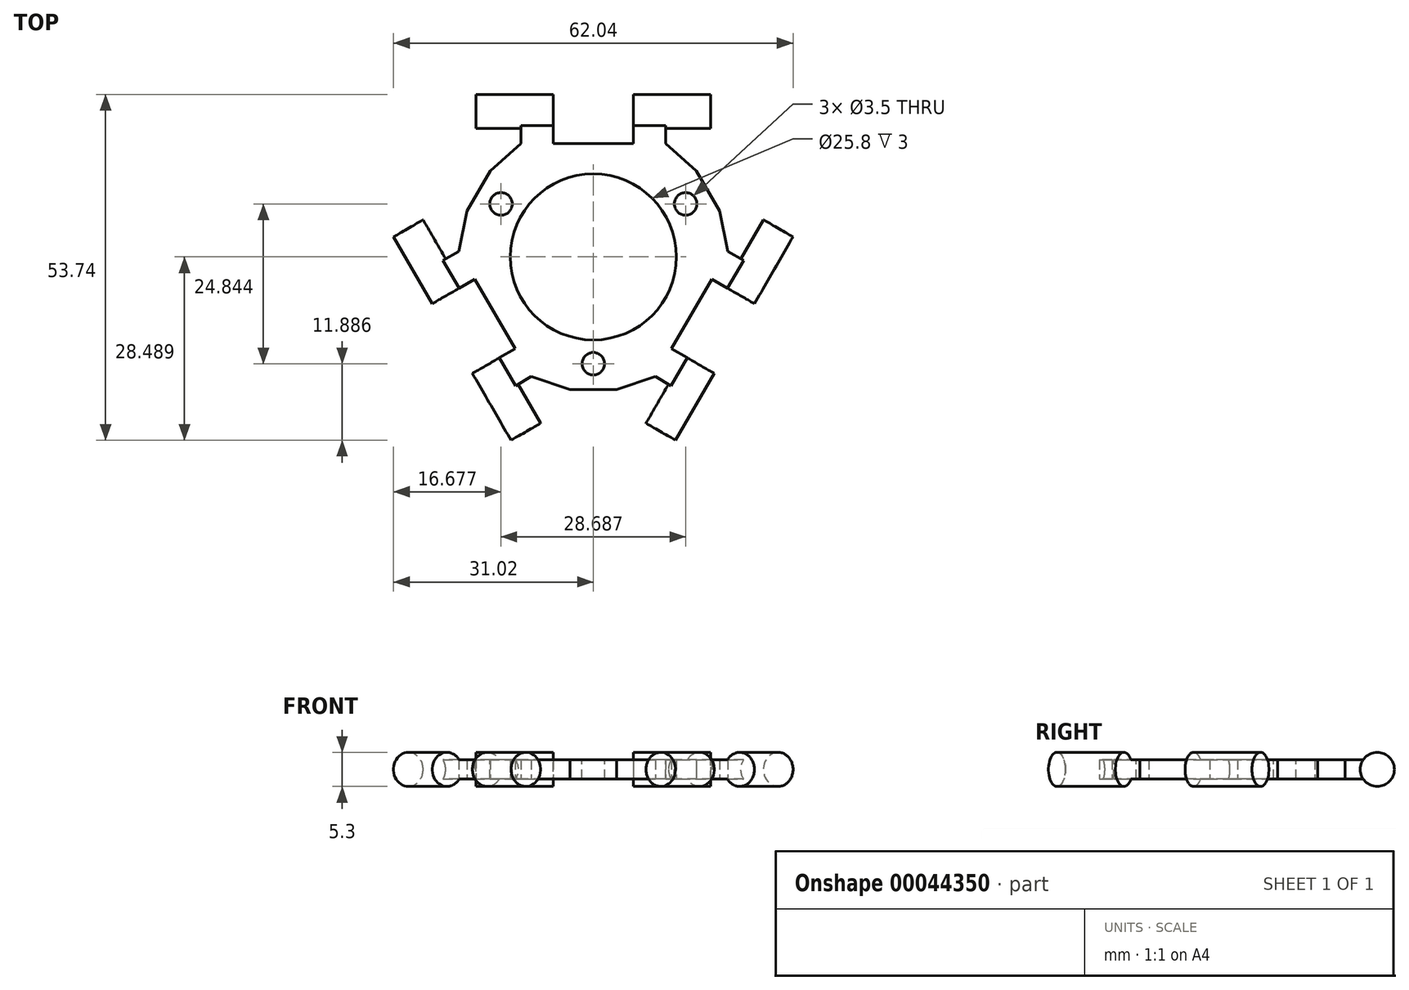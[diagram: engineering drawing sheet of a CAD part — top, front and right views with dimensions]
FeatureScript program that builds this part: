
annotation { "Feature Type Name" : "Feature", "Feature Type Description" : "" }
export const myFeature = defineFeature(function(context is Context, id is Id, definition is map)
    precondition{}
    {
        {
            var Q0;
            Q0=qCreatedBy(makeId("Top.planeOp"),FACE);
            var sketch = newSketch(context, id + "F0", { "sketchPlane" : qUnion([Q0])});
            skLineSegment(sketch, "E0", {"start": v(11.25, 26.96) * mm, "end": v(11.25, 31.96) * mm});
            skLineSegment(sketch, "E1", {"start": v(11.25, 31.96) * mm, "end": v(6.25, 31.96) * mm});
            skLineSegment(sketch, "E2", {"start": v(6.25, 31.96) * mm, "end": v(6.25, 26.96) * mm});
            skLineSegment(sketch, "E3", {"start": v(6.25, 26.96) * mm, "end": v(-6.25, 26.96) * mm});
            skLineSegment(sketch, "E4", {"start": v(-6.25, 26.96) * mm, "end": v(-6.25, 31.96) * mm});
            skLineSegment(sketch, "E5", {"start": v(-6.25, 31.96) * mm, "end": v(-11.25, 31.96) * mm});
            skLineSegment(sketch, "E6", {"start": v(-11.25, 31.96) * mm, "end": v(-11.25, 26.96) * mm});
            skLineSegment(sketch, "E7", {"start": v(11.25, 26.96) * mm, "end": v(16, 22.72) * mm});
            skLineSegment(sketch, "E8", {"start": v(-11.25, 26.96) * mm, "end": v(-16, 22.72) * mm});
            skLineSegment(sketch, "E9", {"start": v(16, 22.72) * mm, "end": v(19.6, 16.48) * mm});
            skLineSegment(sketch, "E10", {"start": v(-16, 22.72) * mm, "end": v(-19.6, 16.48) * mm});
            skLineSegment(sketch, "E11", {"start": v(-19.6, 16.48) * mm, "end": v(-20.9, 10.24) * mm});
            skLineSegment(sketch, "E12", {"start": v(19.6, 16.48) * mm, "end": v(20.9, 10.24) * mm});
            skLineSegment(sketch, "E13", {"start": v(-20.9, 10.24) * mm, "end": v(-25.23, 7.74) * mm});
            skLineSegment(sketch, "E14", {"start": v(-25.23, 7.74) * mm, "end": v(-22.73, 3.41) * mm});
            skLineSegment(sketch, "E15", {"start": v(-22.73, 3.41) * mm, "end": v(-18.4, 5.91) * mm});
            skLineSegment(sketch, "E16", {"start": v(-18.4, 5.91) * mm, "end": v(-12.15, -4.91) * mm});
            skLineSegment(sketch, "E17", {"start": v(-12.15, -4.91) * mm, "end": v(-16.48, -7.41) * mm});
            skLineSegment(sketch, "E18", {"start": v(-16.48, -7.41) * mm, "end": v(-13.98, -11.74) * mm});
            skLineSegment(sketch, "E19", {"start": v(-13.98, -11.74) * mm, "end": v(-9.65, -9.24) * mm});
            skLineSegment(sketch, "E20", {"start": v(20.9, 10.24) * mm, "end": v(25.23, 7.74) * mm});
            skLineSegment(sketch, "E21", {"start": v(25.23, 7.74) * mm, "end": v(22.73, 3.41) * mm});
            skLineSegment(sketch, "E22", {"start": v(22.73, 3.41) * mm, "end": v(18.4, 5.91) * mm});
            skLineSegment(sketch, "E23", {"start": v(18.4, 5.91) * mm, "end": v(12.15, -4.91) * mm});
            skLineSegment(sketch, "E24", {"start": v(12.15, -4.91) * mm, "end": v(16.48, -7.41) * mm});
            skLineSegment(sketch, "E25", {"start": v(16.48, -7.41) * mm, "end": v(13.98, -11.74) * mm});
            skLineSegment(sketch, "E26", {"start": v(13.98, -11.74) * mm, "end": v(9.65, -9.24) * mm});
            skLineSegment(sketch, "E27", {"start": v(-9.65, -9.24) * mm, "end": v(-3.6, -11.24) * mm});
            skLineSegment(sketch, "E28", {"start": v(-3.6, -11.24) * mm, "end": v(3.6, -11.24) * mm});
            skLineSegment(sketch, "E29", {"start": v(3.6, -11.24) * mm, "end": v(9.65, -9.24) * mm});
            skPoint(sketch, "E30.first.point", {"position": v(0, 26.96) * mm});
            skPoint(sketch, "E30.second.point", {"position": v(15.27, 0.5) * mm});
            skPoint(sketch, "E30.third.point", {"position": v(-15.27, 0.5) * mm});
            skCircle(sketch, "E31", {"center": v(0, 9.36) * mm, "radius": 12.9 * mm});
            skLineSegment(sketch, "E32", {"start": v(-17.8, 19.6) * mm, "end": v(15.27, 0.5) * mm, "construction": true});
            skLineSegment(sketch, "E33", {"start": v(17.8, 19.6) * mm, "end": v(-15.27, 0.5) * mm, "construction": true});
            skLineSegment(sketch, "E34", {"start": v(0, -11.24) * mm, "end": v(0, 26.96) * mm, "construction": true});
            skSolve(sketch);
        }
        {
            var Q0;
            Q0=qSketchRegion(id+"F0",true);
            extrude(context, id + "F1", {"entities" : qUnion([Q0]), "depth" : 3 * mm});
        }
        {
            var Q0;
            Q0=makeQuery(id+"F1.opExtrude","CAP_FACE",FACE,{"disambiguationData":[OSD([sQuery(id+"F0.wireOp",EDGE,"E0"),sQuery(id+"F0.wireOp",EDGE,"E1"),sQuery(id+"F0.wireOp",EDGE,"E2"),sQuery(id+"F0.wireOp",EDGE,"E3"),sQuery(id+"F0.wireOp",EDGE,"E4"),sQuery(id+"F0.wireOp",EDGE,"E5"),sQuery(id+"F0.wireOp",EDGE,"E6"),sQuery(id+"F0.wireOp",EDGE,"E7"),sQuery(id+"F0.wireOp",EDGE,"E8"),sQuery(id+"F0.wireOp",EDGE,"E9"),sQuery(id+"F0.wireOp",EDGE,"E10"),sQuery(id+"F0.wireOp",EDGE,"E11"),sQuery(id+"F0.wireOp",EDGE,"E12"),sQuery(id+"F0.wireOp",EDGE,"E13"),sQuery(id+"F0.wireOp",EDGE,"E14"),sQuery(id+"F0.wireOp",EDGE,"E15"),sQuery(id+"F0.wireOp",EDGE,"E16"),sQuery(id+"F0.wireOp",EDGE,"E17"),sQuery(id+"F0.wireOp",EDGE,"E18"),sQuery(id+"F0.wireOp",EDGE,"E19"),sQuery(id+"F0.wireOp",EDGE,"E20"),sQuery(id+"F0.wireOp",EDGE,"E21"),sQuery(id+"F0.wireOp",EDGE,"E22"),sQuery(id+"F0.wireOp",EDGE,"E23"),sQuery(id+"F0.wireOp",EDGE,"E24"),sQuery(id+"F0.wireOp",EDGE,"E25"),sQuery(id+"F0.wireOp",EDGE,"E26"),sQuery(id+"F0.wireOp",EDGE,"E27"),sQuery(id+"F0.wireOp",EDGE,"E28"),sQuery(id+"F0.wireOp",EDGE,"E29"),sQuery(id+"F0.wireOp",EDGE,"E31")])],"isStart":false});
            var sketch = newSketch(context, id + "F2", { "sketchPlane" : qUnion([Q0])});
            skCircle(sketch, "E35", {"center": v(-14.34, 17.6) * mm, "radius": 1.75 * mm});
            skCircle(sketch, "E36", {"center": v(14.34, 17.6) * mm, "radius": 1.75 * mm});
            skCircle(sketch, "E37", {"center": v(0, -7.24) * mm, "radius": 1.75 * mm});
            skLineSegment(sketch, "E38", {"start": v(0, -7.24) * mm, "end": v(3.6, -11.24) * mm, "construction": true});
            skLineSegment(sketch, "E39", {"start": v(0, -7.24) * mm, "end": v(-3.6, -11.24) * mm, "construction": true});
            skLineSegment(sketch, "E40", {"start": v(16, 22.72) * mm, "end": v(14.34, 17.6) * mm, "construction": true});
            skLineSegment(sketch, "E41", {"start": v(19.6, 16.48) * mm, "end": v(14.34, 17.6) * mm, "construction": true});
            skLineSegment(sketch, "E42", {"start": v(-16, 22.72) * mm, "end": v(-14.34, 17.6) * mm, "construction": true});
            skLineSegment(sketch, "E43", {"start": v(-19.6, 16.48) * mm, "end": v(-14.34, 17.6) * mm, "construction": true});
            skLineSegment(sketch, "E44", {"start": v(-14.34, 17.6) * mm, "end": v(14.34, 17.6) * mm, "construction": true});
            skLineSegment(sketch, "E45", {"start": v(14.34, 17.6) * mm, "end": v(0, -7.24) * mm, "construction": true});
            skLineSegment(sketch, "E46", {"start": v(0, -7.24) * mm, "end": v(-14.34, 17.6) * mm, "construction": true});
            skSolve(sketch);
        }
        {
            var Q0;
            Q0=qSketchRegion(id+"F2",true);
            extrude(context, id + "F3", {"entities" : qUnion([Q0]), "operationType" : NewBodyOperationType.REMOVE, "endBound" : BoundingType.THROUGH_ALL, "oppositeDirection" : true, "depth" : 25 * mm});
        }
        {
            var Q0;
            Q0=makeQuery(id+"F1.opExtrude","SWEPT_FACE",FACE,{"disambiguationData":[OSD([sQuery(id+"F0.wireOp",EDGE,"E2")])]});
            var sketch = newSketch(context, id + "F4", { "sketchPlane" : qUnion([Q0])});
            skCircle(sketch, "E47", {"center": v(-31.96, 1.5) * mm, "radius": 2.65 * mm});
            skSolve(sketch);
        }
        {
            var Q0;
            Q0=qSketchRegion(id+"F4",true);
            var Q1;
            Q1=makeQuery(id+"F1.opExtrude","SWEPT_FACE",FACE,{"disambiguationData":[OSD([sQuery(id+"F0.wireOp",EDGE,"E0")])]});
            extrude(context, id + "F5", {"entities" : qUnion([Q0]), "operationType" : NewBodyOperationType.ADD, "oppositeDirection" : true, "endBoundEntityFace" : qUnion([Q1]), "depth" : 12 * mm});
        }
        {
            var Q0;
            Q0=makeQuery(id+"F1.opExtrude","SWEPT_FACE",FACE,{"disambiguationData":[OSD([sQuery(id+"F0.wireOp",EDGE,"E4")])]});
            var sketch = newSketch(context, id + "F6", { "sketchPlane" : qUnion([Q0])});
            skCircle(sketch, "E48", {"center": v(31.96, 1.5) * mm, "radius": 2.65 * mm});
            skSolve(sketch);
        }
        {
            var Q0;
            Q0=qSketchRegion(id+"F6",true);
            extrude(context, id + "F7", {"entities" : qUnion([Q0]), "operationType" : NewBodyOperationType.ADD, "oppositeDirection" : true, "depth" : 12 * mm});
        }
        {
            var Q0;
            Q0=makeQuery(id+"F1.opExtrude","SWEPT_FACE",FACE,{"disambiguationData":[OSD([sQuery(id+"F0.wireOp",EDGE,"E15")])]});
            var sketch = newSketch(context, id + "F8", { "sketchPlane" : qUnion([Q0])});
            skCircle(sketch, "E49", {"center": v(-17.98, 1.5) * mm, "radius": 2.65 * mm});
            skSolve(sketch);
        }
        {
            var Q0;
            Q0=qSketchRegion(id+"F8",true);
            extrude(context, id + "F9", {"entities" : qUnion([Q0]), "operationType" : NewBodyOperationType.ADD, "oppositeDirection" : true, "depth" : 12 * mm});
        }
        {
            var Q0;
            Q0=makeQuery(id+"F1.opExtrude","SWEPT_FACE",FACE,{"disambiguationData":[OSD([sQuery(id+"F0.wireOp",EDGE,"E17")])]});
            var sketch = newSketch(context, id + "F10", { "sketchPlane" : qUnion([Q0])});
            skCircle(sketch, "E50", {"center": v(17.98, 1.5) * mm, "radius": 2.65 * mm});
            skSolve(sketch);
        }
        {
            var Q0;
            Q0=qSketchRegion(id+"F10",true);
            extrude(context, id + "F11", {"entities" : qUnion([Q0]), "operationType" : NewBodyOperationType.ADD, "oppositeDirection" : true, "depth" : 12 * mm});
        }
        {
            var Q0;
            Q0=makeQuery(id+"F1.opExtrude","SWEPT_FACE",FACE,{"disambiguationData":[OSD([sQuery(id+"F0.wireOp",EDGE,"E24")])]});
            var sketch = newSketch(context, id + "F12", { "sketchPlane" : qUnion([Q0])});
            skCircle(sketch, "E51", {"center": v(-17.98, 1.5) * mm, "radius": 2.65 * mm});
            skSolve(sketch);
        }
        {
            var Q0;
            Q0=qSketchRegion(id+"F12",true);
            extrude(context, id + "F13", {"entities" : qUnion([Q0]), "operationType" : NewBodyOperationType.ADD, "oppositeDirection" : true, "depth" : 12 * mm});
        }
        {
            var Q0;
            Q0=makeQuery(id+"F1.opExtrude","SWEPT_FACE",FACE,{"disambiguationData":[OSD([sQuery(id+"F0.wireOp",EDGE,"E22")])]});
            var sketch = newSketch(context, id + "F14", { "sketchPlane" : qUnion([Q0])});
            skCircle(sketch, "E52", {"center": v(17.98, 1.5) * mm, "radius": 2.65 * mm});
            skSolve(sketch);
        }
        {
            var Q0;
            Q0=qSketchRegion(id+"F14",true);
            extrude(context, id + "F15", {"entities" : qUnion([Q0]), "operationType" : NewBodyOperationType.ADD, "oppositeDirection" : true, "depth" : 12 * mm});
        }
    });
